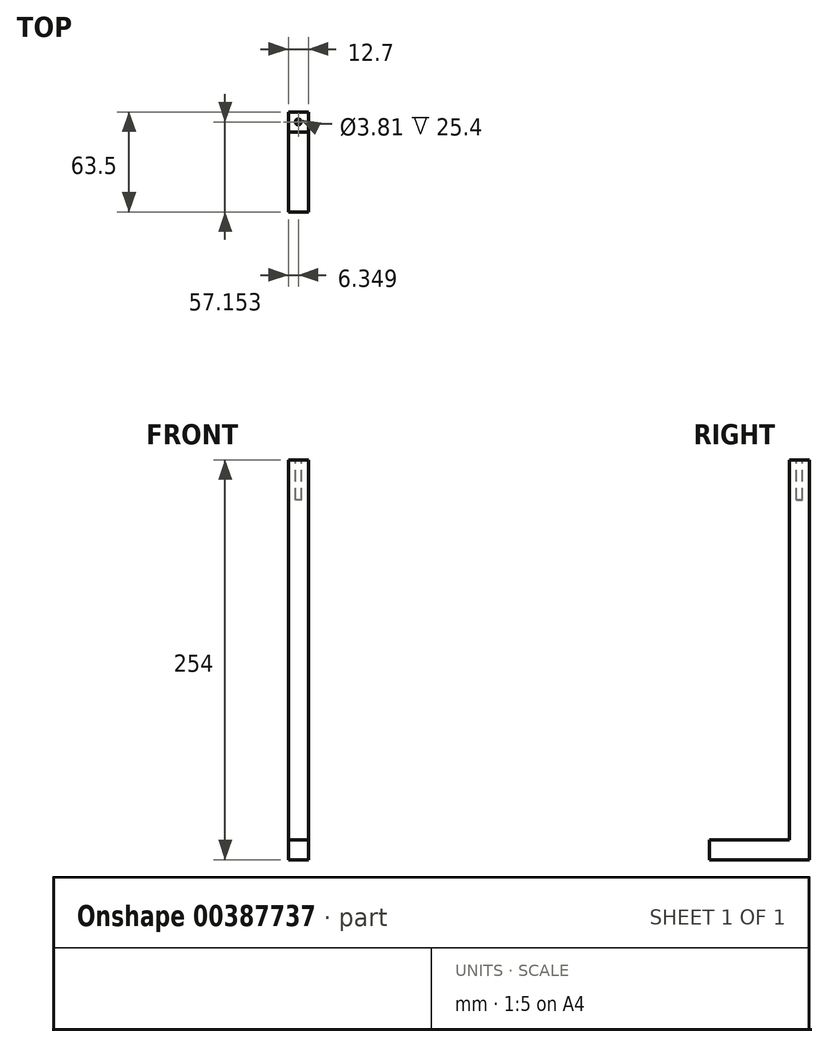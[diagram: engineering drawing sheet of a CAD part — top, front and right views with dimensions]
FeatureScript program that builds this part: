
annotation { "Feature Type Name" : "Feature", "Feature Type Description" : "" }
export const myFeature = defineFeature(function(context is Context, id is Id, definition is map)
    precondition{}
    {
        {
            var Q0;
            Q0=qCreatedBy(makeId("Right.planeOp"),FACE);
            var sketch = newSketch(context, id + "F0", { "sketchPlane" : qUnion([Q0])});
            skLineSegment(sketch, "E0.bottom", {"start": v(-98.32, -75.28) * mm, "end": v(3.28, -75.28) * mm});
            skLineSegment(sketch, "E0.top", {"start": v(-98.32, -81.63) * mm, "end": v(3.28, -81.63) * mm});
            skLineSegment(sketch, "E0.left", {"start": v(-98.32, -75.28) * mm, "end": v(-98.32, -81.63) * mm});
            skLineSegment(sketch, "E0.right", {"start": v(3.28, -75.28) * mm, "end": v(3.28, -81.63) * mm});
            skLineSegment(sketch, "E1.bottom", {"start": v(3.28, -75.28) * mm, "end": v(-3.07, -75.28) * mm});
            skLineSegment(sketch, "E1.top", {"start": v(3.28, 128.25) * mm, "end": v(-3.07, 128.25) * mm});
            skLineSegment(sketch, "E1.left", {"start": v(3.28, -75.28) * mm, "end": v(3.28, 128.25) * mm});
            skLineSegment(sketch, "E1.right", {"start": v(-3.07, -75.28) * mm, "end": v(-3.07, 128.25) * mm});
            skSolve(sketch);
        }
        {
            var Q0;
            Q0 = qSketchRegion(id + "F0", true);
            extrude(context, id + "F1", {"entities" : qUnion([Q0]), "depth" : 101.6 * mm});
        }
        {
            var Q0;
            Q0=makeQuery(id+"F1.opExtrude","SWEPT_FACE",FACE,{"disambiguationData":[OSD([sQuery(id+"F0.wireOp",EDGE,"E0.bottom")])]});
            var sketch = newSketch(context, id + "F2", { "sketchPlane" : qUnion([Q0])});
            skLineSegment(sketch, "E2.bottom", {"start": v(0, -98.32) * mm, "end": v(101.6, -98.32) * mm});
            skLineSegment(sketch, "E2.top", {"start": v(0, -91.97) * mm, "end": v(101.6, -91.97) * mm});
            skLineSegment(sketch, "E2.left", {"start": v(0, -98.32) * mm, "end": v(0, -91.97) * mm});
            skLineSegment(sketch, "E2.right", {"start": v(101.6, -98.32) * mm, "end": v(101.6, -91.97) * mm});
            skSolve(sketch);
        }
        {
            var Q0;
            Q0 = qSketchRegion(id + "F2", true);
            extrude(context, id + "F3", {"entities" : qUnion([Q0]), "operationType" : NewBodyOperationType.ADD, "depth" : 25.4 * mm});
        }
        {
            var Q0;
            Q0=makeQuery(id+"F1.opExtrude","SWEPT_BODY",BODY,{"disambiguationData":[OSD([sQuery(id+"F0.wireOp",EDGE,"E0.bottom"),sQuery(id+"F0.wireOp",EDGE,"E0.top"),sQuery(id+"F0.wireOp",EDGE,"E0.left"),sQuery(id+"F0.wireOp",EDGE,"E0.right"),sQuery(id+"F0.wireOp",EDGE,"E1.top"),sQuery(id+"F0.wireOp",EDGE,"E1.left"),sQuery(id+"F0.wireOp",EDGE,"E1.right")])]});
            deleteBodies(context, id + "F4", {"entities" : qUnion([Q0])});
        }
        {
            var Q0;
            Q0=qCreatedBy(makeId("Top.planeOp"),FACE);
            var sketch = newSketch(context, id + "F5", { "sketchPlane" : qUnion([Q0])});
            skLineSegment(sketch, "E3.bottom", {"start": v(-39.13, 23.23) * mm, "end": v(-26.43, 23.23) * mm});
            skLineSegment(sketch, "E3.top", {"start": v(-39.13, 10.53) * mm, "end": v(-26.43, 10.53) * mm});
            skLineSegment(sketch, "E3.left", {"start": v(-39.13, 23.23) * mm, "end": v(-39.13, 10.53) * mm});
            skLineSegment(sketch, "E3.right", {"start": v(-26.43, 23.23) * mm, "end": v(-26.43, 10.53) * mm});
            skSolve(sketch);
        }
        {
            var Q0;
            Q0 = qSketchRegion(id + "F5", true);
            extrude(context, id + "F6", {"entities" : qUnion([Q0]), "depth" : 254 * mm});
        }
        {
            var Q0;
            Q0=makeQuery(id+"F6.opExtrude","CAP_FACE",FACE,{"disambiguationData":[OSD([sQuery(id+"F5.wireOp",EDGE,"E3.bottom"),sQuery(id+"F5.wireOp",EDGE,"E3.top"),sQuery(id+"F5.wireOp",EDGE,"E3.left"),sQuery(id+"F5.wireOp",EDGE,"E3.right")])],"isStart":false});
            var sketch = newSketch(context, id + "F7", { "sketchPlane" : qUnion([Q0])});
            skCircle(sketch, "E4", {"center": v(-32.78, 16.88) * mm, "radius": 1.9 * mm});
            skSolve(sketch);
        }
        {
            var Q0;
            Q0 = qSketchRegion(id + "F7", true);
            extrude(context, id + "F8", {"entities" : qUnion([Q0]), "operationType" : NewBodyOperationType.REMOVE, "oppositeDirection" : true, "depth" : 25.4 * mm});
        }
        {
            var Q0;
            Q0=makeQuery(id+"F6.opExtrude","SWEPT_FACE",FACE,{"disambiguationData":[OSD([sQuery(id+"F5.wireOp",EDGE,"E3.top")])]});
            var sketch = newSketch(context, id + "F9", { "sketchPlane" : qUnion([Q0])});
            skLineSegment(sketch, "E5.bottom", {"start": v(-39.13, 0) * mm, "end": v(-26.43, 0) * mm});
            skLineSegment(sketch, "E5.top", {"start": v(-39.13, 12.7) * mm, "end": v(-26.43, 12.7) * mm});
            skLineSegment(sketch, "E5.left", {"start": v(-39.13, 0) * mm, "end": v(-39.13, 12.7) * mm});
            skLineSegment(sketch, "E5.right", {"start": v(-26.43, 0) * mm, "end": v(-26.43, 12.7) * mm});
            skSolve(sketch);
        }
        {
            var Q0;
            Q0=makeQuery(id+"F9.imprint","IMPRINT",FACE,{"disambiguationData":[TD([[makeQuery(id+"F9.imprint","IMPRINT",EDGE,{"derivedFrom":sQuery(id+"F9.wireOp",EDGE,"E5.bottom")}),1.0]])]});
            extrude(context, id + "F10", {"entities" : qUnion([Q0]), "operationType" : NewBodyOperationType.ADD, "depth" : 50.8 * mm});
        }
    });
